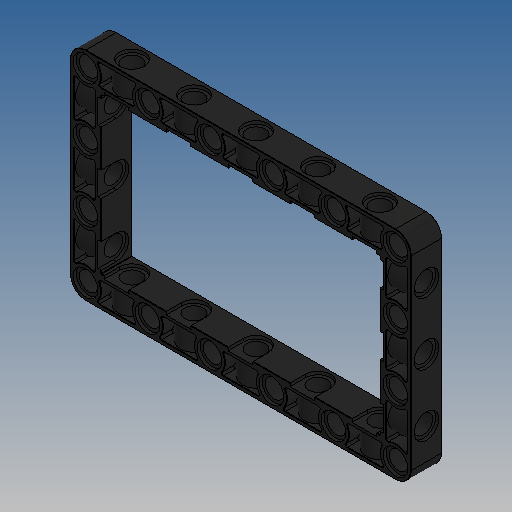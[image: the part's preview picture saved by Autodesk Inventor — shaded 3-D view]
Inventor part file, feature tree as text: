
AUTODESK INVENTOR PART (.ipt)
format: ipt  version: 2025 (Build 290162010, 162A)  size: 1,200,128 bytes
history: native  units: mm
features: sketch x13, extrude x11, pattern_linear x4, fillet x3, mirror x3, hole x2, projected_geometry x2
ambient origin geometry x8: Origin, YZ Plane, XZ Plane, XY Plane, X Axis, Y Axis, Z Axis, Center Point
bodies: Volumenkörper1 (feature_tree)
feature tree (38):
  extrude  "Extrusion1"  Depth=40.0mm
  fillet  "Rundung1"  Radius=24.0mm
  extrude  "Extrusion2"  Depth=8.0mm
  extrude  "Extrusion3"  Depth=4.0mm
  pattern_linear  "Rechteckige Anordnung1"  Count1=3 Spacing1=16.0mm
  pattern_linear  "Rechteckige Anordnung2"  Count1=2 Spacing1=16.0mm
  mirror  "Spiegeln1"
  extrude  "Extrusion4"  Depth=0.4mm
  extrude  "Extrusion8"  Depth=3.1mm TaperAngle=0.0deg
  fillet  "Rundung2"  Radius=0.1mm
  extrude  "Extrusion6"  Depth=7.2mm
  hole  "Bohrung1"  [1 undecoded]
  extrude  "Extrusion9"  Depth=16.0mm
  pattern_linear  "Rechteckige Anordnung3"  Spacing1=3.1mm  [1 undecoded]
  extrude  "Extrusion5"  TaperAngle=0.0deg  [1 undecoded]
  extrude  "Extrusion10"  Depth=0.8mm TaperAngle=0.0deg
  fillet  "Rundung3"  Radius=0.6mm
  extrude  "Extrusion11"  Depth=0.6mm
  hole  "Bohrung2"  [1 undecoded]
  extrude  "Extrusion12"  Depth=0.1mm
  pattern_linear  "Rechteckige Anordnung4"  Spacing1=7.2mm  [1 undecoded]
  mirror  "Spiegeln4"
  mirror  "Spiegeln5"
  sketch  "Skizze1"  dims[d0=4.0mm d1=40.0mm d2=24.0mm]
  sketch  "Skizze2"  dims[d3=0.1mm d4=8.0mm]
  sketch  "Skizze3"  dims[d5=8.0mm d6=4.0mm]
  sketch  "Skizze4"  dims[d7=0.0mm]
  sketch  "Skizze5"  dims[d8=6.4mm]
  sketch  "Skizze6"  dims[d9=0.8mm d10=0.0mm]
  sketch  "Skizze7"  dims[d11=4.8mm]
  sketch  "Skizze9"  dims[d12=0.8mm d13=0.0mm d14=30.0mm d16=16.0mm d17=20.0mm d19=16.0mm]
  projected_geometry  "Projizierte Kontur1"
  sketch  "Skizze10"  dims[d20=1.0mm d21=0.4mm]
  sketch  "Skizze11"  dims[d22=3.1mm d23=0.0mm d25=3.1mm d26=0.0mm d27=0.1mm]
  projected_geometry  "Projizierte Kontur2"
  sketch  "Skizze12"  dims[d28=0.1mm d29=7.2mm]
  sketch  "Skizze13"  dims[d30=10.0mm d31=0.0mm]
  sketch  "Skizze14"  dims[d32=4.8mm d33=6.0mm d34=6.4mm d35=0.8mm d36=90.0deg d37=8.0mm d38=20.594885mm d42=30.0mm d44=16.0mm d45=3.1mm d46=0.0mm d50=0.8mm d51=0.0mm d52=0.6mm d53=0.6mm d54=3.1mm d55=0.0mm d56=0.1mm d57=7.2mm d58=3.1mm d59=0.0mm d60=4.8mm d61=6.0mm d62=6.4mm d63=0.8mm d64=90.0deg d65=8.0mm d66=20.594885mm d67=0.8mm d68=0.0mm d69=20.0mm d71=16.0mm]
note: 5 required parameter values undecoded (feature->parameter linkage not recoverable at this tier; creation-order binding heuristic only, values carry confidence <= 0.55)
